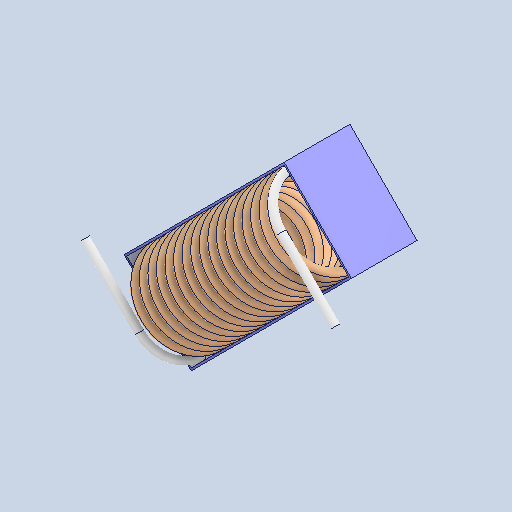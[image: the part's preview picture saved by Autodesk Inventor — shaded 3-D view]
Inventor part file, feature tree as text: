
AUTODESK INVENTOR PART (.ipt)
format: ipt  version: 2025 (Build 290162000, 162)  size: 708,608 bytes
history: native  units: mm
features: sweep x1, other x1
ambient origin geometry x8: Origin, YZ Plane, XZ Plane, XY Plane, X Axis, Y Axis, Z Axis, Center Point
bodies: Solid1 (feature_tree), Solid2 (feature_tree)
feature tree (2):
  sweep  "Sweep9"
  other  "Cut-Extrude1"
